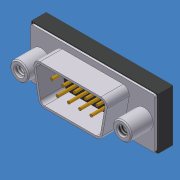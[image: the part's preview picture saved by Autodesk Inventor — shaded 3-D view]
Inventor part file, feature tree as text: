
AUTODESK INVENTOR PART (.ipt)
format: ipt  version: 2011 (Build 150239000, 239)  size: 219,648 bytes
history: native  units: mm (DEFAULTED — no unit token found)
features: sketch x7, extrude x6, mirror x2, hole x1, chamfer x1
ambient origin geometry x8: Origin, YZ Plane, XZ Plane, XY Plane, X Axis, Y Axis, Z Axis, Center Point
bodies: Solid1 (feature_tree)
feature tree (17):
  extrude  "Extrusion1"  Depth=9.96mm
  extrude  "Extrusion2"  Depth=30.81mm
  extrude  "Extrusion3"  Depth=12.58mm
  extrude  "Extrusion4"  Depth=17.453293mm
  extrude  "Extrusion5"  Depth=1.0mm
  hole  "Hole2"  [1 undecoded]
  chamfer  "Chamfer2"  Distance=0.5mm
  mirror  "Mirror2"
  extrude  "Extrusion6"  Depth=5.9mm TaperAngle=0.0deg
  mirror  "Mirror3"
  sketch  "Sketch1"  dims[d0=16.96mm d1=9.96mm]
  sketch  "Sketch2"  dims[d2=3.6mm d3=30.81mm]
  sketch  "Sketch5"  dims[d4=0.0001mm d5=0.0mm d6=12.58mm]
  sketch  "Sketch6"  dims[d7=3.6mm d8=0.0mm d22=17.453293mm]
  sketch  "Sketch7"  dims[d23=17.453293mm d24=1.0mm]
  sketch  "Sketch8"  dims[d25=1.0mm d26=8.25mm]
  sketch  "Sketch9"  dims[d27=16.79mm d29=0.5mm d30=5.9mm d31=0.0mm d32=0.25mm d33=0.5mm d34=0.5mm d35=0.0mm d36=4.5mm d37=2.91mm d38=5.4mm d39=0.0mm d40=2.156mm d41=6.0mm d42=4.0mm d43=2.0mm d44=14.3117mm d45=8.0mm d46=20.594885mm d47=0.25mm d48=2.0mm d49=2.84mm d50=1.37mm d51=0.67mm d52=30.0mm d54=2.74mm d55=10.0mm d57=10.0mm d59=5.0mm d60=0.0mm d61=45.0deg]
note: 1 required parameter value undecoded (feature->parameter linkage not recoverable at this tier; creation-order binding heuristic only, values carry confidence <= 0.55)
